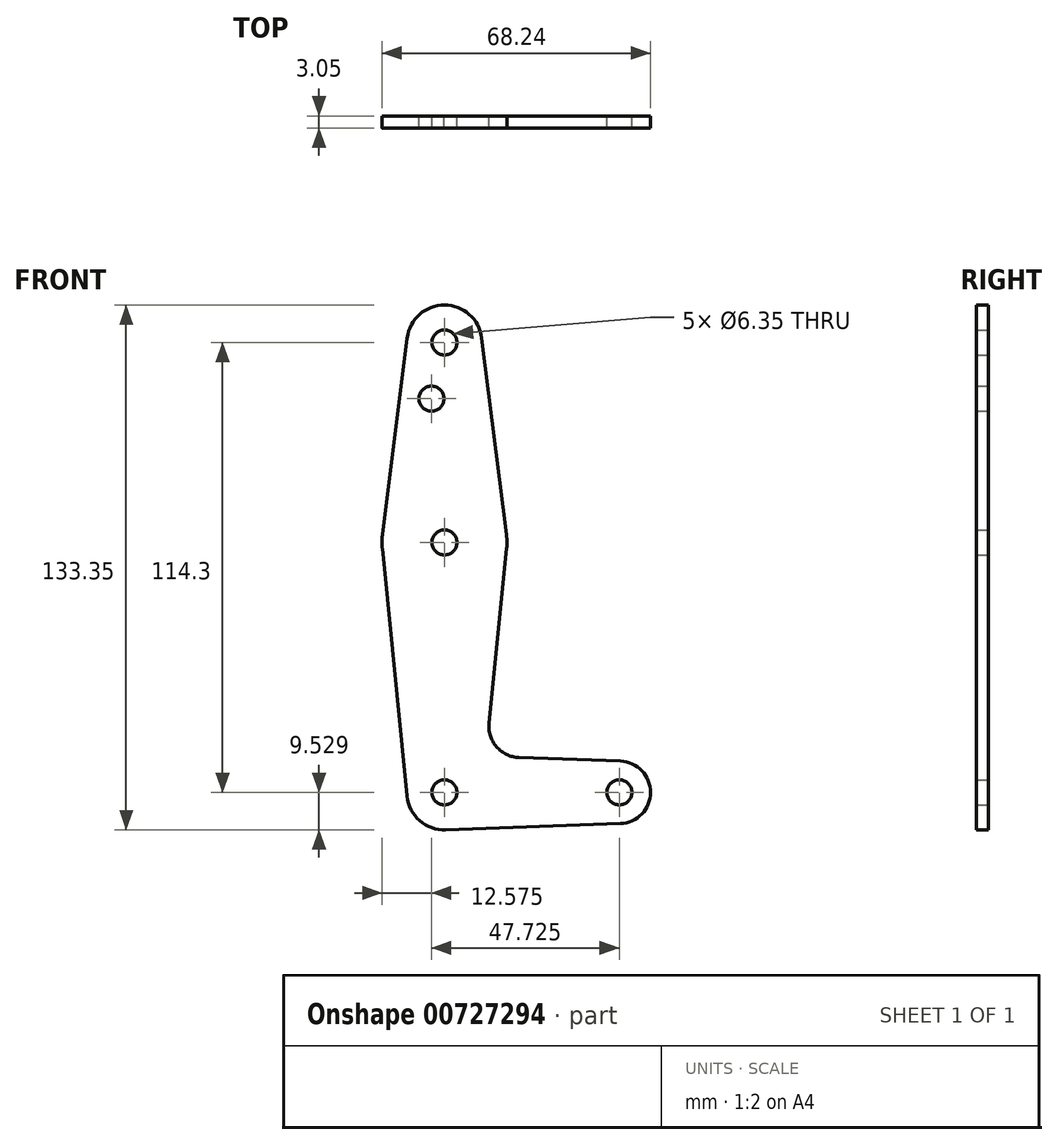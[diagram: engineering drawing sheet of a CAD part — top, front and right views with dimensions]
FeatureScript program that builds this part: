
annotation { "Feature Type Name" : "Feature", "Feature Type Description" : "" }
export const myFeature = defineFeature(function(context is Context, id is Id, definition is map)
    precondition{}
    {
        {
            var Q0;
            Q0=qCreatedBy(makeId("Front.planeOp"),FACE);
            var sketch = newSketch(context, id + "F0", { "sketchPlane" : qUnion([Q0])});
            skLineSegment(sketch, "E0", {"start": v(-60.6, -60.14) * mm, "end": v(-16.16, -60.14) * mm, "construction": true});
            skCircle(sketch, "E1", {"center": v(-60.58, 54.16) * mm, "radius": 9.53 * mm});
            skCircle(sketch, "E2", {"center": v(-60.6, -60.14) * mm, "radius": 9.53 * mm});
            skCircle(sketch, "E3", {"center": v(-16.16, -60.14) * mm, "radius": 7.94 * mm});
            skCircle(sketch, "E4", {"center": v(-60.58, 3.36) * mm, "radius": 15.88 * mm});
            skLineSegment(sketch, "E5", {"start": v(-70.03, 55.35) * mm, "end": v(-76.33, 5.34) * mm});
            skLineSegment(sketch, "E6", {"start": v(-51.13, 55.35) * mm, "end": v(-44.83, 5.34) * mm});
            skLineSegment(sketch, "E7", {"start": v(-44.79, 1.76) * mm, "end": v(-49.26, -42.54) * mm});
            skLineSegment(sketch, "E8", {"start": v(-76.38, 1.78) * mm, "end": v(-70.09, -61.09) * mm});
            skLineSegment(sketch, "E9", {"start": v(-41.63, -51.29) * mm, "end": v(-15.88, -52.2) * mm});
            skLineSegment(sketch, "E10", {"start": v(-60.27, -69.66) * mm, "end": v(-15.88, -68.07) * mm});
            skCircle(sketch, "E11", {"center": v(-60.58, 54.16) * mm, "radius": 3.18 * mm});
            skCircle(sketch, "E12", {"center": v(-60.58, 3.36) * mm, "radius": 3.18 * mm});
            skCircle(sketch, "E13", {"center": v(-60.6, -60.14) * mm, "radius": 3.18 * mm});
            skCircle(sketch, "E14", {"center": v(-16.16, -60.14) * mm, "radius": 3.18 * mm});
            skArc(sketch, "E15.filletArc", {"start": v(-49.26, -42.54) * mm, "mid": v(-47.34, -48.57) * mm, "end": v(-41.63, -51.29) * mm});
            skLineSegment(sketch, "E16", {"start": v(-60.58, 54.16) * mm, "end": v(-60.58, 3.36) * mm});
            skCircle(sketch, "E17", {"center": v(-63.89, 39.88) * mm, "radius": 3.18 * mm});
            skSolve(sketch);
        }
        {
            var Q0;
            Q0 = qSketchRegion(id + "F0", true);
            extrude(context, id + "F1", {"entities" : qUnion([Q0]), "depth" : 3.05 * mm, "offsetDistance" : 25.4 * mm});
        }
    });
